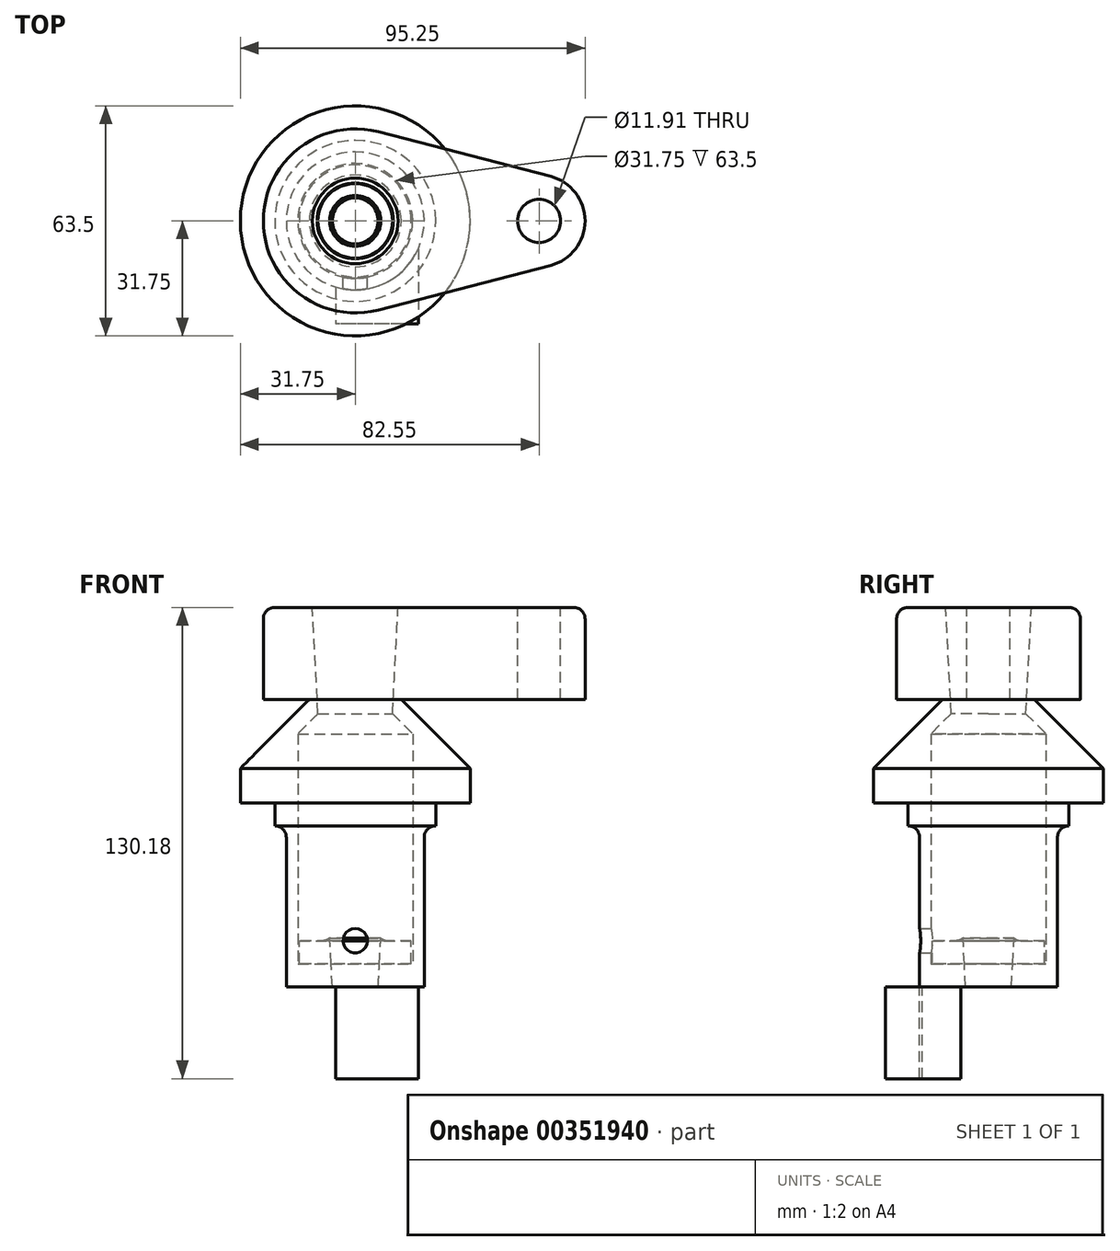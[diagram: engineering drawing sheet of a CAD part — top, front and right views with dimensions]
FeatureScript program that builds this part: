
annotation { "Feature Type Name" : "Feature", "Feature Type Description" : "" }
export const myFeature = defineFeature(function(context is Context, id is Id, definition is map)
    precondition{}
    {
        {
            var Q0;
            Q0=qCreatedBy(makeId("Front.planeOp"),FACE);
            var sketch = newSketch(context, id + "F0", { "sketchPlane" : qUnion([Q0])});
            skLineSegment(sketch, "E0", {"start": v(0, 0) * mm, "end": v(19.05, 0) * mm});
            skLineSegment(sketch, "E1", {"start": v(19.05, 0) * mm, "end": v(19.05, 44.45) * mm});
            skLineSegment(sketch, "E2", {"start": v(19.05, 44.45) * mm, "end": v(22.23, 44.45) * mm});
            skLineSegment(sketch, "E3", {"start": v(22.23, 44.45) * mm, "end": v(22.23, 50.8) * mm});
            skLineSegment(sketch, "E4", {"start": v(22.23, 50.8) * mm, "end": v(31.75, 50.8) * mm});
            skLineSegment(sketch, "E5", {"start": v(31.75, 50.8) * mm, "end": v(31.75, 60.32) * mm});
            skLineSegment(sketch, "E6", {"start": v(31.75, 60.32) * mm, "end": v(12.7, 79.38) * mm});
            skLineSegment(sketch, "E7", {"start": v(12.7, 79.38) * mm, "end": v(0, 79.38) * mm});
            skLineSegment(sketch, "E8", {"start": v(0, 79.38) * mm, "end": v(0, 0) * mm});
            skLineSegment(sketch, "E9", {"start": v(6.35, 79.38) * mm, "end": v(15.87, 69.85) * mm});
            skLineSegment(sketch, "E10", {"start": v(15.87, 69.85) * mm, "end": v(15.88, 6.35) * mm});
            skLineSegment(sketch, "E11", {"start": v(15.88, 6.35) * mm, "end": v(0, 6.35) * mm});
            skLineSegment(sketch, "E12", {"start": v(0, 79.38) * mm, "end": v(0, 86.88) * mm, "construction": true});
            skLineSegment(sketch, "E13", {"start": v(5.95, 104.78) * mm, "end": v(5.95, 12.7) * mm});
            skLineSegment(sketch, "E14", {"start": v(5.95, 12.7) * mm, "end": v(15.48, 12.7) * mm});
            skLineSegment(sketch, "E15", {"start": v(15.48, 12.7) * mm, "end": v(15.48, 6.35) * mm});
            skLineSegment(sketch, "E16", {"start": v(5.95, 104.78) * mm, "end": v(0, 104.78) * mm});
            skLineSegment(sketch, "E17", {"start": v(0, 104.78) * mm, "end": v(0, 79.38) * mm});
            skSolve(sketch);
        }
        {
            var Q0;
            {var subQ1=sQuery(id+"F0.wireOp",EDGE,"E0");Q0=makeQuery(id+"F0.imprint","IMPRINT",FACE,{"disambiguationData":[TD([[makeQuery(id+"F0.imprint","IMPRINT",EDGE,{"derivedFrom":subQ1}),1.0]])]});}
            var Q1;
            Q1=sQuery(id+"F0.wireOp",EDGE,"E8");
            revolve(context, id + "F1", {"entities" : qUnion([Q0]), "axis" : qUnion([Q1]), "revolveType" : RevolveType.FULL, "oppositeDirection" : true});
        }
        {
            var Q0;
            {var subQ4=sQuery(id+"F0.wireOp",EDGE,"E16");Q0=makeQuery(id+"F0.imprint","IMPRINT",FACE,{"disambiguationData":[TD([[makeQuery(id+"F0.imprint","IMPRINT",EDGE,{"derivedFrom":subQ4}),1.0]])]});}
            var Q1;
            {var subQ0=sQuery(id+"F0.wireOp",EDGE,"E14");Q1=makeQuery(id+"F0.imprint","IMPRINT",FACE,{"disambiguationData":[TD([[makeQuery(id+"F0.imprint","IMPRINT",EDGE,{"derivedFrom":subQ0}),-1.0]])]});}
            var Q2;
            Q2=sQuery(id+"F0.wireOp",EDGE,"E17");
            revolve(context, id + "F2", {"entities" : qUnion([Q0, Q1]), "axis" : qUnion([Q2]), "revolveType" : RevolveType.FULL});
        }
        {
            var Q0;
            Q0=makeQuery(id+"F2.opRevolve","SWEPT_FACE",FACE,{"disambiguationData":[OSD([sQuery(id+"F0.wireOp",EDGE,"E16")])]});
            var sketch = newSketch(context, id + "F3", { "sketchPlane" : qUnion([Q0])});
            skCircle(sketch, "E18", {"center": v(0, 0) * mm, "radius": 25.4 * mm});
            skCircle(sketch, "E19", {"center": v(50.8, 0) * mm, "radius": 12.7 * mm});
            skLineSegment(sketch, "E20", {"start": v(53.98, 12.3) * mm, "end": v(6.35, 24.6) * mm});
            skLineSegment(sketch, "E21", {"start": v(53.98, -12.3) * mm, "end": v(6.35, -24.6) * mm});
            skCircle(sketch, "E22.0", {"center": v(0, 0) * mm, "radius": 5.95 * mm});
            skCircle(sketch, "E23", {"center": v(50.8, 0) * mm, "radius": 5.95 * mm});
            skSolve(sketch);
        }
        {
            var Q0;
            Q0 = qSketchRegion(id + "F3", true);
            var Q1;
            Q1=makeQuery(id+"F1.opRevolve","SWEPT_FACE",FACE,{"disambiguationData":[OSD([sQuery(id+"F0.wireOp",EDGE,"E7")])]});
            extrude(context, id + "F4", {"entities" : qUnion([Q0]), "oppositeDirection" : true, "endBoundEntityFace" : qUnion([Q1]), "depth" : 25.4 * mm});
        }
        {
            var Q0;
            Q0=qCreatedBy(makeId("Front.planeOp"),FACE);
            var sketch = newSketch(context, id + "F5", { "sketchPlane" : qUnion([Q0])});
            skPoint(sketch, "E24", {"position": v(0, 12.7) * mm});
            skSolve(sketch);
        }
        {
            var Q0;
            Q0=sQuery(id+"F5.wireOp",VERTEX,"E24");
            var Q1;
            Q1=makeQuery(id+"F1.opRevolve","SWEPT_BODY",BODY,{"disambiguationData":[OSD([sQuery(id+"F0.wireOp",EDGE,"E0"),sQuery(id+"F0.wireOp",EDGE,"E1"),sQuery(id+"F0.wireOp",EDGE,"E2"),sQuery(id+"F0.wireOp",EDGE,"E3"),sQuery(id+"F0.wireOp",EDGE,"E4"),sQuery(id+"F0.wireOp",EDGE,"E5"),sQuery(id+"F0.wireOp",EDGE,"E6"),sQuery(id+"F0.wireOp",EDGE,"E7"),sQuery(id+"F0.wireOp",EDGE,"E8"),sQuery(id+"F0.wireOp",EDGE,"E9"),sQuery(id+"F0.wireOp",EDGE,"E10"),sQuery(id+"F0.wireOp",EDGE,"E11")])]});
            hole(context, id + "F6", {"style" : HoleStyle.SIMPLE, "endStyle" : HoleEndStyle.THROUGH, "oppositeDirection" : true, "standardTappedOrClearance" : lookupTablePath({ "standard" : "ANSI", "fit" : "Normal (ASME)", "size" : "1/4", "type" : "Clearance" }), "standardBlindInLast" : lookupTablePath({ "fit" : "Free", "standard" : "ANSI", "size" : "1/4", "type" : "Clearance" }), "holeDiameter" : 6.76 * mm, "isTappedThrough" : true, "tappedDepth" : 8.9 * mm, "tapClearance" : 3, "locations" : qUnion([Q0]), "scope" : qUnion([Q1])});
        }
        {
            var Q0;
            Q0=makeQuery(id+"F4.opExtrude","CAP_EDGE",EDGE,{"disambiguationData":[OSD([sQuery(id+"F3.wireOp",EDGE,"E21")])],"isStart":true});
            var Q1;
            Q1=makeQuery(id+"F1.opRevolve","SWEPT_EDGE",EDGE,{"disambiguationData":[OSD([sQuery(id+"F0.wireOp",EDGE,"E1"),sQuery(id+"F0.wireOp",EDGE,"E2")])]});
            var Q2;
            Q2=makeQuery(id+"F2.opRevolve","SWEPT_EDGE",EDGE,{"disambiguationData":[OSD([sQuery(id+"F0.wireOp",EDGE,"E13"),sQuery(id+"F0.wireOp",EDGE,"E14")])]});
            fillet(context, id + "F7", {"entities" : qUnion([Q0, Q1, Q2]), "radius" : 3.17 * mm, "tangentPropagation" : true, "allowEdgeOverflow" : false});
        }
        {
            var Q0;
            Q0=makeQuery(id+"F1.opRevolve","SWEPT_FACE",FACE,{"disambiguationData":[OSD([sQuery(id+"F0.wireOp",EDGE,"E0")])]});
            var sketch = newSketch(context, id + "F8", { "sketchPlane" : qUnion([Q0])});
            skCircle(sketch, "E25", {"center": v(0, 0) * mm, "radius": 6.35 * mm});
            skSolve(sketch);
        }
        {
            var Q0;
            Q0=makeQuery(id+"F8.imprint","IMPRINT",FACE,{"disambiguationData":[TD([[makeQuery(id+"F8.imprint","IMPRINT",EDGE,{"derivedFrom":sQuery(id+"F8.wireOp",EDGE,"E25")}),1.0]])]});
            extrude(context, id + "F9", {"entities" : qUnion([Q0]), "operationType" : NewBodyOperationType.REMOVE, "endBound" : BoundingType.THROUGH_ALL, "oppositeDirection" : true, "depth" : 25.4 * mm, "hasDraft" : true, "draftAngle" : 3 * degree});
        }
        {
            var Q0;
            Q0=makeQuery(id+"F1.opRevolve","SWEPT_FACE",FACE,{"disambiguationData":[OSD([sQuery(id+"F0.wireOp",EDGE,"E0")])]});
            var sketch = newSketch(context, id + "F10", { "sketchPlane" : qUnion([Q0])});
            skLineSegment(sketch, "E26.bottom", {"start": v(17.42, 7.7) * mm, "end": v(-5.37, 7.7) * mm});
            skLineSegment(sketch, "E26.top", {"start": v(17.42, 28.44) * mm, "end": v(-5.37, 28.44) * mm});
            skLineSegment(sketch, "E26.left", {"start": v(17.42, 7.7) * mm, "end": v(17.42, 28.44) * mm});
            skLineSegment(sketch, "E26.right", {"start": v(-5.37, 7.7) * mm, "end": v(-5.37, 28.44) * mm});
            skPoint(sketch, "E26.middle", {"position": v(6.03, 18.07) * mm});
            skSolve(sketch);
        }
        {
            var Q0;
            {var subQ0=sQuery(id+"F10.wireOp",EDGE,"E26.top");Q0=makeQuery(id+"F10.imprint","IMPRINT",FACE,{"disambiguationData":[TD([[makeQuery(id+"F10.imprint","IMPRINT",EDGE,{"derivedFrom":subQ0}),1.0]])]});}
            extrude(context, id + "F11", {"entities" : qUnion([Q0]), "operationType" : NewBodyOperationType.ADD, "depth" : 25.4 * mm});
        }
    });
